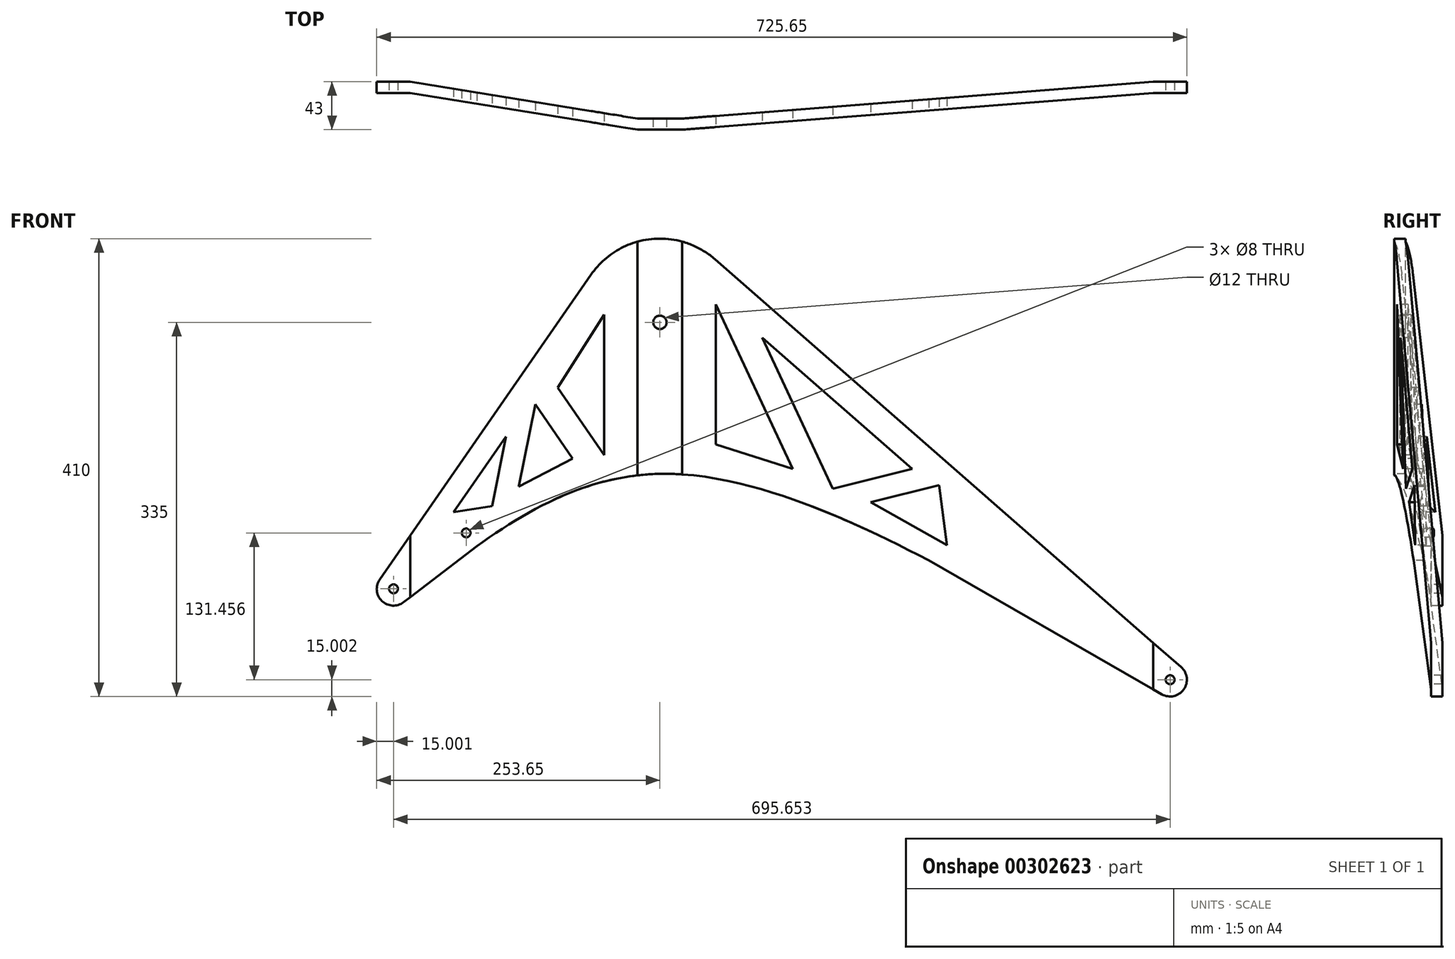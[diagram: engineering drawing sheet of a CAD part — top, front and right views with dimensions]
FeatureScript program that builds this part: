
annotation { "Feature Type Name" : "Feature", "Feature Type Description" : "" }
export const myFeature = defineFeature(function(context is Context, id is Id, definition is map)
    precondition{}
    {
        {
            var Q0;
            Q0=qCreatedBy(makeId("Front.planeOp"),FACE);
            var sketch = newSketch(context, id + "F0", { "sketchPlane" : qUnion([Q0])});
            skCircle(sketch, "E0", {"center": v(0, 0) * mm, "radius": 5 * mm});
            skCircle(sketch, "E1", {"center": v(-238.65, -238.65) * mm, "radius": 4 * mm});
            skCircle(sketch, "E2", {"center": v(457, -320) * mm, "radius": 4 * mm});
            skLineSegment(sketch, "E3", {"start": v(-238.65, -238.65) * mm, "end": v(0, 0) * mm});
            skLineSegment(sketch, "E4", {"start": v(0, 0) * mm, "end": v(457, -320) * mm});
            skLineSegment(sketch, "E5", {"start": v(0, 0) * mm, "end": v(0, -238.65) * mm});
            skLineSegment(sketch, "E6", {"start": v(0, -238.65) * mm, "end": v(-238.65, -238.65) * mm});
            skLineSegment(sketch, "E7", {"start": v(0, -238.65) * mm, "end": v(0, -320) * mm});
            skLineSegment(sketch, "E8", {"start": v(0, -320) * mm, "end": v(457, -320) * mm});
            skSolve(sketch);
        }
        {
            var Q0;
            Q0=qCreatedBy(makeId("Top.planeOp"),FACE);
            var sketch = newSketch(context, id + "F1", { "sketchPlane" : qUnion([Q0])});
            skLineSegment(sketch, "E9.bottom", {"start": v(-20, 0) * mm, "end": v(20, 0) * mm});
            skLineSegment(sketch, "E9.top", {"start": v(-20, -10) * mm, "end": v(20, -10) * mm});
            skLineSegment(sketch, "E9.left", {"start": v(-20, 0) * mm, "end": v(-20, -10) * mm});
            skLineSegment(sketch, "E9.right", {"start": v(20, 0) * mm, "end": v(20, -10) * mm});
            skLineSegment(sketch, "E10", {"start": v(472, 23) * mm, "end": v(472, 33) * mm});
            skLineSegment(sketch, "E11", {"start": v(-253.65, 23) * mm, "end": v(-253.65, 33) * mm});
            skLineSegment(sketch, "E12", {"start": v(472, 33) * mm, "end": v(442, 33) * mm});
            skLineSegment(sketch, "E13", {"start": v(442, 33) * mm, "end": v(442, 23) * mm});
            skLineSegment(sketch, "E14", {"start": v(442, 23) * mm, "end": v(472, 23) * mm});
            skLineSegment(sketch, "E15", {"start": v(-253.65, 33) * mm, "end": v(-223.65, 33) * mm});
            skLineSegment(sketch, "E16", {"start": v(-223.65, 33) * mm, "end": v(-223.65, 23) * mm});
            skLineSegment(sketch, "E17", {"start": v(-223.65, 23) * mm, "end": v(-253.65, 23) * mm});
            skLineSegment(sketch, "E18", {"start": v(-223.65, 23) * mm, "end": v(-20, -10) * mm});
            skLineSegment(sketch, "E19", {"start": v(-20, 0) * mm, "end": v(-223.65, 33) * mm});
            skLineSegment(sketch, "E20", {"start": v(20, 0) * mm, "end": v(442, 33) * mm});
            skLineSegment(sketch, "E21", {"start": v(442, 23) * mm, "end": v(20, -10) * mm});
            skLineSegment(sketch, "E22", {"start": v(0, 0) * mm, "end": v(0, 130) * mm});
            skLineSegment(sketch, "E23", {"start": v(0, 65) * mm, "end": v(-332.58, 65) * mm});
            skSolve(sketch);
        }
        {
            var Q0;
            Q0 = qSketchRegion(id + "F1", true);
            extrude(context, id + "F2", {"entities" : qUnion([Q0]), "oppositeDirection" : true, "depth" : 340 * mm});
        }
        {
            var Q0;
            Q0 = qSketchRegion(id + "F1", true);
            extrude(context, id + "F3", {"entities" : qUnion([Q0]), "operationType" : NewBodyOperationType.ADD, "depth" : 100 * mm});
        }
        {
            var Q0;
            Q0=qCreatedBy(makeId("Front.planeOp"),FACE);
            var sketch = newSketch(context, id + "F4", { "sketchPlane" : qUnion([Q0])});
            skCircle(sketch, "E24", {"center": v(-238.65, -238.65) * mm, "radius": 15 * mm});
            skCircle(sketch, "E25", {"center": v(457, -320) * mm, "radius": 15 * mm});
            skCircle(sketch, "E26", {"center": v(0, 0) * mm, "radius": 75 * mm});
            skLineSegment(sketch, "E27", {"start": v(-264.4, -249.44) * mm, "end": v(-11, 115.7) * mm});
            skLineSegment(sketch, "E28", {"start": v(12.3, 88.89) * mm, "end": v(551.26, -382.5) * mm});
            skLineSegment(sketch, "E29", {"start": v(0, -75) * mm, "end": v(-229.54, -250.56) * mm});
            skLineSegment(sketch, "E30", {"start": v(0, -75) * mm, "end": v(449.54, -333) * mm});
            skFitSpline(sketch, "E31", {"points": [v(-229.54, -250.56) * mm, v(0, -135.64) * mm, v(449.54, -333) * mm], "startDerivative": vector(454.74, 347.81) * mm, "endDerivative": vector(744.11, -427.08) * mm});
            skSolve(sketch);
        }
        {
            var Q0;
            Q0 = qSketchRegion(id + "F4", true);
            extrude(context, id + "F5", {"entities" : qUnion([Q0]), "operationType" : NewBodyOperationType.INTERSECT, "endBound" : BoundingType.SYMMETRIC, "oppositeDirection" : true, "depth" : 152 * mm});
        }
        {
            var Q0;
            {var subQ0=sQuery(id+"F1.wireOp",EDGE,"E9.top");Q0=makeQuery(id+"F3.boolean.opBoolean","MERGE",FACE,{"derivedFrom":[makeQuery(id+"F2.opExtrude","SWEPT_FACE",FACE,{"disambiguationData":[OSD([subQ0])]}),makeQuery(id+"F3.opExtrude","SWEPT_FACE",FACE,{"disambiguationData":[OSD([subQ0])]})]});}
            var sketch = newSketch(context, id + "F6", { "sketchPlane" : qUnion([Q0])});
            skLineSegment(sketch, "E32", {"start": v(-50, 6.88) * mm, "end": v(-50, -118.87) * mm});
            skLineSegment(sketch, "E33", {"start": v(-50, -118.87) * mm, "end": v(-91.57, -58.59) * mm});
            skLineSegment(sketch, "E34", {"start": v(-91.57, -58.59) * mm, "end": v(-50, 6.88) * mm});
            skLineSegment(sketch, "E35", {"start": v(-78.26, -121.92) * mm, "end": v(-111.7, -73.42) * mm});
            skLineSegment(sketch, "E36", {"start": v(-111.7, -73.42) * mm, "end": v(-126.47, -146.98) * mm});
            skLineSegment(sketch, "E37", {"start": v(-126.47, -146.98) * mm, "end": v(-78.26, -121.92) * mm});
            skLineSegment(sketch, "E38", {"start": v(-137.89, -102.22) * mm, "end": v(-150.41, -164.65) * mm});
            skLineSegment(sketch, "E39", {"start": v(-184.86, -169.92) * mm, "end": v(-137.89, -102.22) * mm});
            skLineSegment(sketch, "E40", {"start": v(50, -109.34) * mm, "end": v(50, 16.05) * mm});
            skLineSegment(sketch, "E41", {"start": v(50, 16.05) * mm, "end": v(118.97, -131.23) * mm});
            skLineSegment(sketch, "E42", {"start": v(118.97, -131.23) * mm, "end": v(50, -109.34) * mm});
            skLineSegment(sketch, "E43", {"start": v(91.49, -13.6) * mm, "end": v(154.91, -149.03) * mm});
            skLineSegment(sketch, "E44", {"start": v(154.91, -149.03) * mm, "end": v(225.97, -131.22) * mm});
            skLineSegment(sketch, "E45", {"start": v(225.97, -131.22) * mm, "end": v(91.49, -13.6) * mm});
            skLineSegment(sketch, "E46", {"start": v(188.86, -161.14) * mm, "end": v(250.2, -145.76) * mm});
            skLineSegment(sketch, "E47", {"start": v(250.2, -145.76) * mm, "end": v(257, -199.36) * mm});
            skLineSegment(sketch, "E48", {"start": v(257, -199.36) * mm, "end": v(188.86, -161.14) * mm});
            skLineSegment(sketch, "E49", {"start": v(-184.86, -169.92) * mm, "end": v(-150.41, -164.65) * mm});
            skCircle(sketch, "E50", {"center": v(-238.65, -238.65) * mm, "radius": 4 * mm});
            skCircle(sketch, "E51", {"center": v(457, -320) * mm, "radius": 4 * mm});
            skCircle(sketch, "E52", {"center": v(0, 0) * mm, "radius": 6 * mm});
            skCircle(sketch, "E53", {"center": v(-173.55, -188.54) * mm, "radius": 4 * mm});
            skSolve(sketch);
        }
        {
            var Q0;
            Q0 = qSketchRegion(id + "F6", true);
            extrude(context, id + "F7", {"entities" : qUnion([Q0]), "operationType" : NewBodyOperationType.REMOVE, "endBound" : BoundingType.SYMMETRIC, "oppositeDirection" : true, "depth" : 132 * mm});
        }
    });
